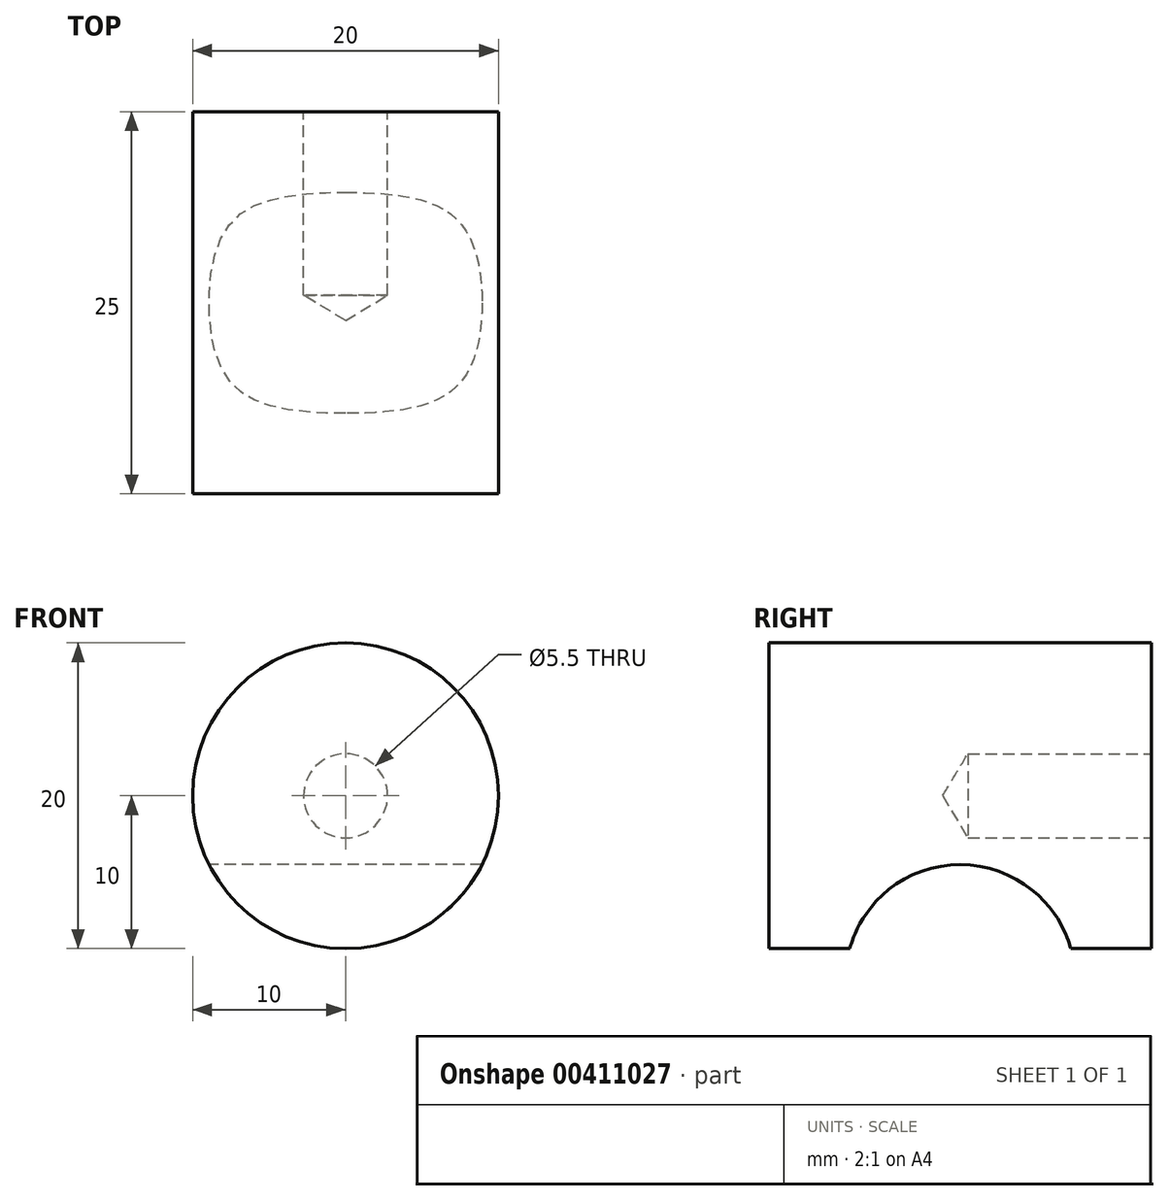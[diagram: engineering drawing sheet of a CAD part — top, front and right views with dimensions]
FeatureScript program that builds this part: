
annotation { "Feature Type Name" : "Feature", "Feature Type Description" : "" }
export const myFeature = defineFeature(function(context is Context, id is Id, definition is map)
    precondition{}
    {
        {
            var Q0;
            Q0=qCreatedBy(makeId("Front.planeOp"),FACE);
            var sketch = newSketch(context, id + "F0", { "sketchPlane" : qUnion([Q0])});
            skCircle(sketch, "E0", {"center": v(0, 0) * mm, "radius": 10 * mm});
            skSolve(sketch);
        }
        {
            var Q0;
            Q0 = qSketchRegion(id + "F0", true);
            extrude(context, id + "F1", {"entities" : qUnion([Q0]), "depth" : 25 * mm});
        }
        {
            var Q0;
            Q0=qCreatedBy(makeId("Right.planeOp"),FACE);
            var sketch = newSketch(context, id + "F2", { "sketchPlane" : qUnion([Q0])});
            skCircle(sketch, "E1", {"center": v(-12.5, -12) * mm, "radius": 7.5 * mm});
            skPoint(sketch, "E2.start.orphan", {"position": v(0, 0) * mm});
            skLineSegment(sketch, "E3", {"start": v(-12.5, -12) * mm, "end": v(0, -12) * mm, "construction": true});
            skLineSegment(sketch, "E4", {"start": v(0, -12) * mm, "end": v(0, 0) * mm, "construction": true});
            skSolve(sketch);
        }
        {
            var Q0;
            Q0=makeQuery(id+"F2.imprint","IMPRINT",FACE,{"disambiguationData":[TD([[makeQuery(id+"F2.imprint","IMPRINT",EDGE,{"derivedFrom":sQuery(id+"F2.wireOp",EDGE,"E1")}),1.0]])]});
            var Q1;
            Q1=sQuery(id+"F2.wireOp",EDGE,"E1");
            extrude(context, id + "F3", {"entities" : qUnion([Q0]), "operationType" : NewBodyOperationType.REMOVE, "surfaceEntities" : qUnion([Q1]), "endBound" : BoundingType.THROUGH_ALL, "depth" : 25 * mm, "hasSecondDirection" : true, "secondDirectionBound" : SecondDirectionBoundingType.THROUGH_ALL, "secondDirectionOppositeDirection" : true, "secondDirectionDepth" : 25 * mm});
        }
        {
            var Q0;
            Q0=makeQuery(id+"F1.opExtrude","CAP_FACE",FACE,{"disambiguationData":[OSD([sQuery(id+"F0.wireOp",EDGE,"E0")])],"isStart":true});
            var sketch = newSketch(context, id + "F4", { "sketchPlane" : qUnion([Q0])});
            skPoint(sketch, "E5", {"position": v(0, 0) * mm});
            skSolve(sketch);
        }
        {
            var Q0;
            Q0=sQuery(id+"F4.wireOp",VERTEX,"E5");
            var Q1;
            Q1=makeQuery(id+"F1.opExtrude","SWEPT_BODY",BODY,{"disambiguationData":[OSD([sQuery(id+"F0.wireOp",EDGE,"E0")])]});
            hole(context, id + "F5", {"style" : HoleStyle.SIMPLE, "endStyle" : HoleEndStyle.BLIND, "standardTappedOrClearance" : lookupTablePath({ "standard" : "ISO", "fit" : "Normal", "size" : "M5", "type" : "Clearance" }), "standardBlindInLast" : lookupTablePath({ "fit" : "Standard", "standard" : "ISO", "size" : "M5", "type" : "Clearance" }), "holeDiameter" : 5.5 * mm, "holeDepth" : 12 * mm, "isTappedThrough" : true, "tappedDepth" : 12 * mm, "tapClearance" : 3, "locations" : qUnion([Q0]), "scope" : qUnion([Q1])});
        }
    });
